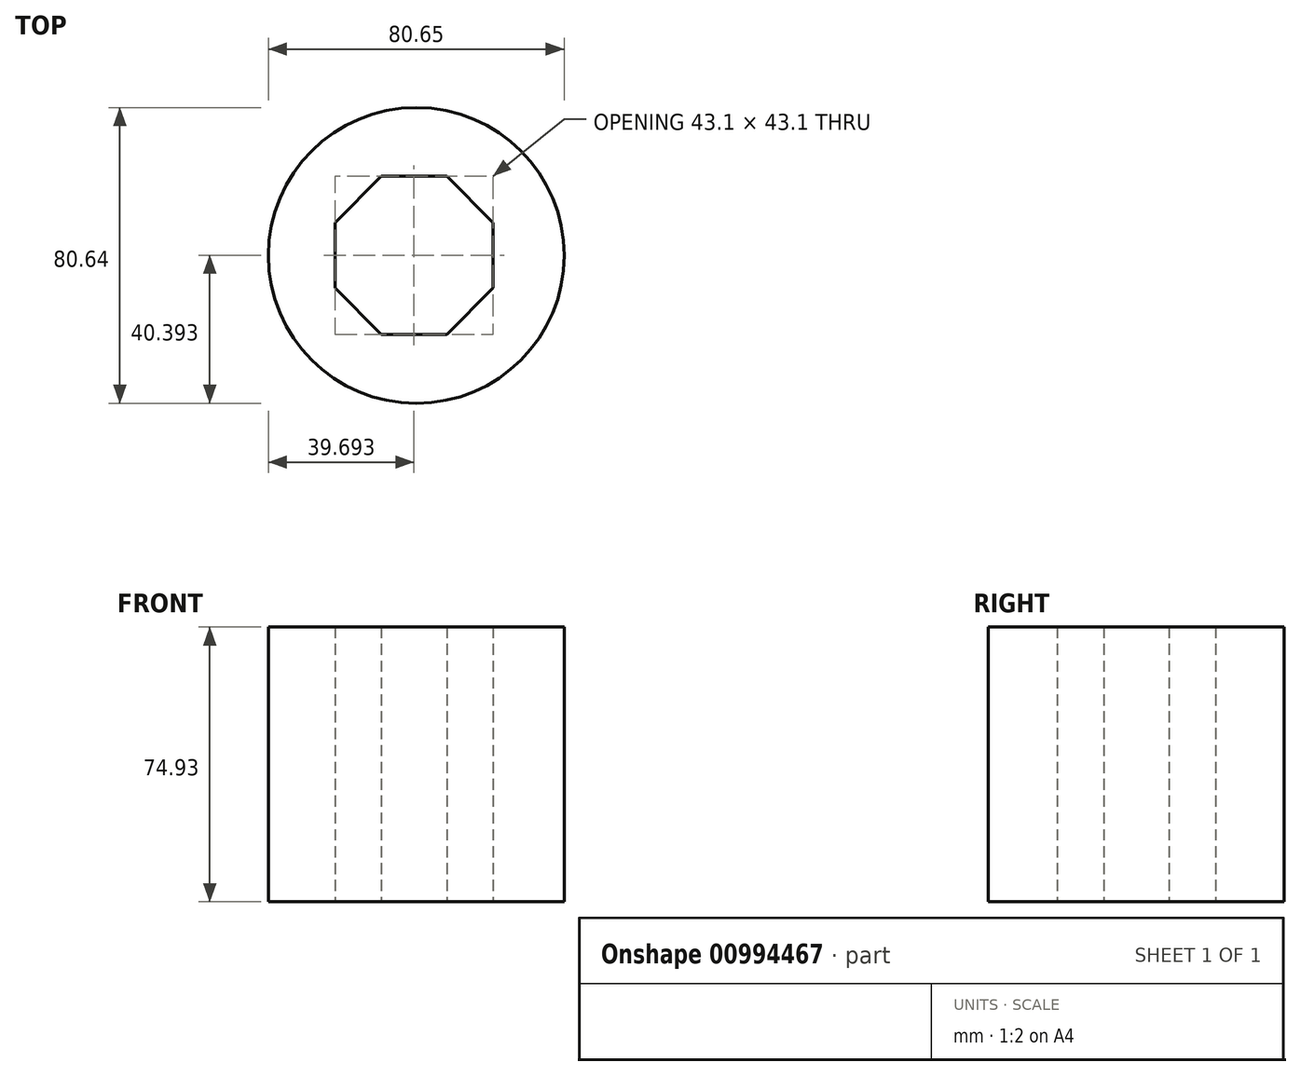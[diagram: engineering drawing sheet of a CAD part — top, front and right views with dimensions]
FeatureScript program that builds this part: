
annotation { "Feature Type Name" : "Feature", "Feature Type Description" : "" }
export const myFeature = defineFeature(function(context is Context, id is Id, definition is map)
    precondition{}
    {
        {
            var Q0;
            Q0=qCreatedBy(makeId("Top.planeOp"),FACE);
            var sketch = newSketch(context, id + "F0", { "sketchPlane" : qUnion([Q0])});
            skCircle(sketch, "E0", {"center": v(-14.8, -26.06) * mm, "radius": 40.32 * mm});
            skSolve(sketch);
        }
        {
            var Q0;
            Q0=makeQuery(id+"F0.imprint","IMPRINT",FACE,{"disambiguationData":[TD([[makeQuery(id+"F0.imprint","IMPRINT",EDGE,{"derivedFrom":sQuery(id+"F0.wireOp",EDGE,"E0")}),1.0]])]});
            var sketch = newSketch(context, id + "F1", { "sketchPlane" : qUnion([Q0])});
            skCircle(sketch, "E1.cCircle", {"center": v(-15.43, -25.99) * mm, "radius": 21.55 * mm, "construction": true});
            skLineSegment(sketch, "E1.0", {"start": v(-36.98, -34.91) * mm, "end": v(-36.98, -17.06) * mm});
            skLineSegment(sketch, "E1.1", {"start": v(-36.98, -17.06) * mm, "end": v(-24.35, -4.43) * mm});
            skLineSegment(sketch, "E1.2", {"start": v(-24.35, -4.43) * mm, "end": v(-6.5, -4.43) * mm});
            skLineSegment(sketch, "E1.3", {"start": v(-6.5, -4.43) * mm, "end": v(6.13, -17.06) * mm});
            skLineSegment(sketch, "E1.4", {"start": v(6.13, -17.06) * mm, "end": v(6.13, -34.91) * mm});
            skLineSegment(sketch, "E1.5", {"start": v(6.13, -34.91) * mm, "end": v(-6.5, -47.54) * mm});
            skLineSegment(sketch, "E1.6", {"start": v(-6.5, -47.54) * mm, "end": v(-24.35, -47.54) * mm});
            skLineSegment(sketch, "E1.7", {"start": v(-24.35, -47.54) * mm, "end": v(-36.98, -34.91) * mm});
            skPoint(sketch, "E1.0.midPoint", {"position": v(-36.98, -25.99) * mm});
            skSolve(sketch);
        }
        {
            var Q0;
            Q0=makeQuery(id+"F1.imprint","IMPRINT",FACE,{"disambiguationData":[TD([[makeQuery(id+"F1.imprint","IMPRINT",EDGE,{"derivedFrom":sQuery(id+"F1.wireOp",EDGE,"E1.0")}),1.0]])]});
            extrude(context, id + "F2", {"entities" : qUnion([Q0]), "depth" : 74.93 * mm, "offsetDistance" : 25.4 * mm});
        }
    });
